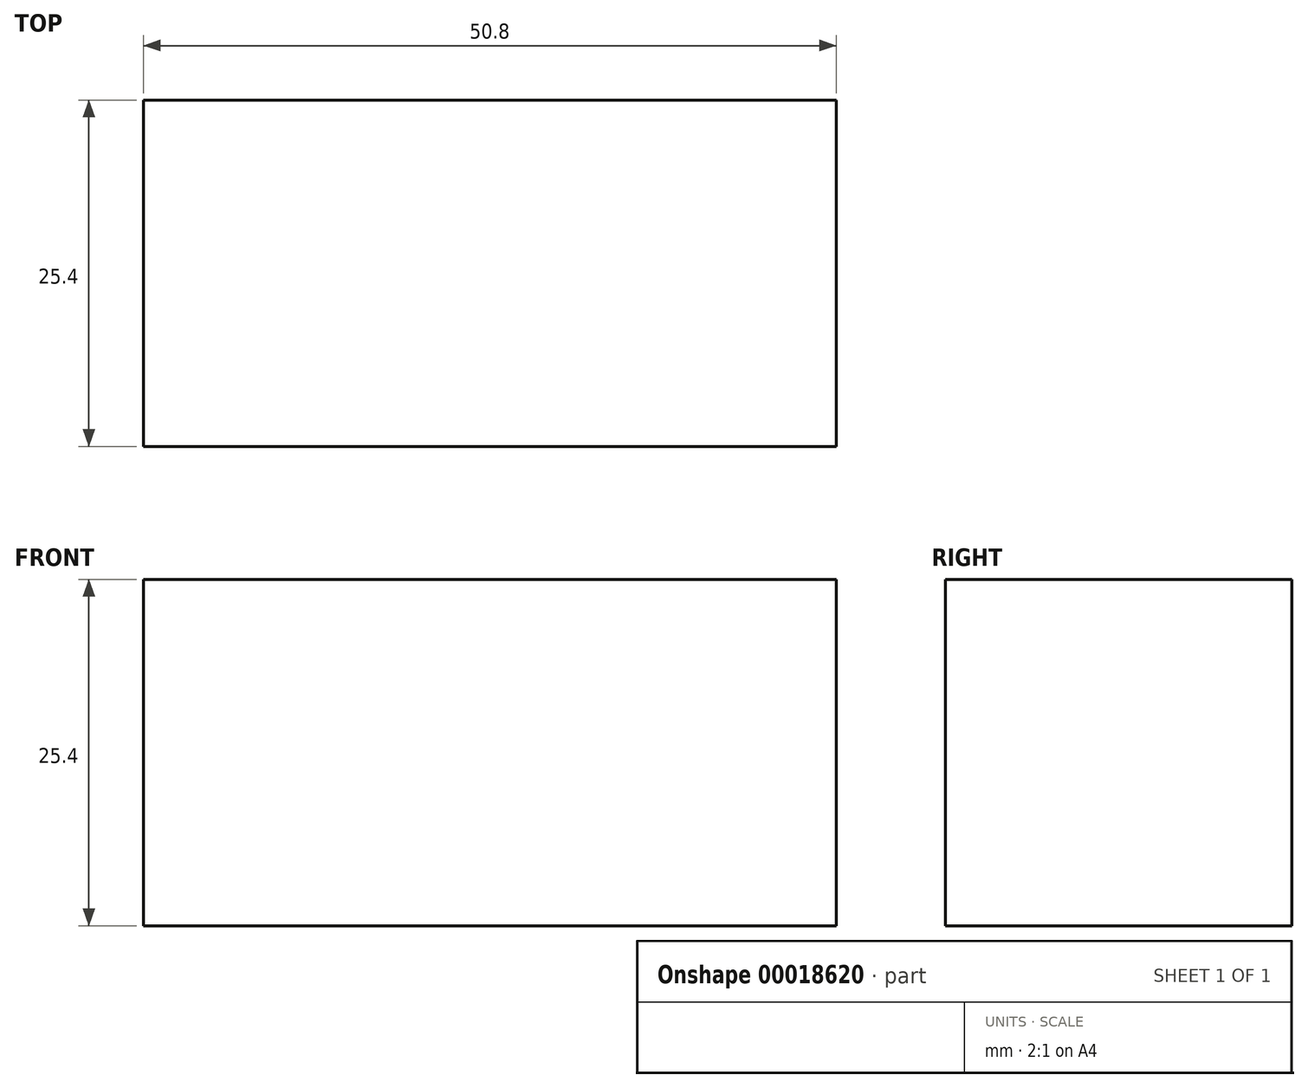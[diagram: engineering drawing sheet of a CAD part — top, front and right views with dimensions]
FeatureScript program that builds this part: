
annotation { "Feature Type Name" : "Feature", "Feature Type Description" : "" }
export const myFeature = defineFeature(function(context is Context, id is Id, definition is map)
    precondition{}
    {
        {
            var Q0;
            Q0=qCreatedBy(makeId("Top.planeOp"),FACE);
            var sketch = newSketch(context, id + "F0", { "sketchPlane" : qUnion([Q0])});
            skLineSegment(sketch, "E0.bottom", {"start": v(0, 0) * mm, "end": v(50.8, 0) * mm});
            skLineSegment(sketch, "E0.top", {"start": v(0, 25.4) * mm, "end": v(50.8, 25.4) * mm});
            skLineSegment(sketch, "E0.left", {"start": v(0, 0) * mm, "end": v(0, 25.4) * mm});
            skLineSegment(sketch, "E0.right", {"start": v(50.8, 0) * mm, "end": v(50.8, 25.4) * mm});
            skSolve(sketch);
        }
        {
            var Q0;
            Q0 = qSketchRegion(id + "F0", true);
            extrude(context, id + "F1", {"entities" : qUnion([Q0]), "depth" : 25.4 * mm});
        }
    });
